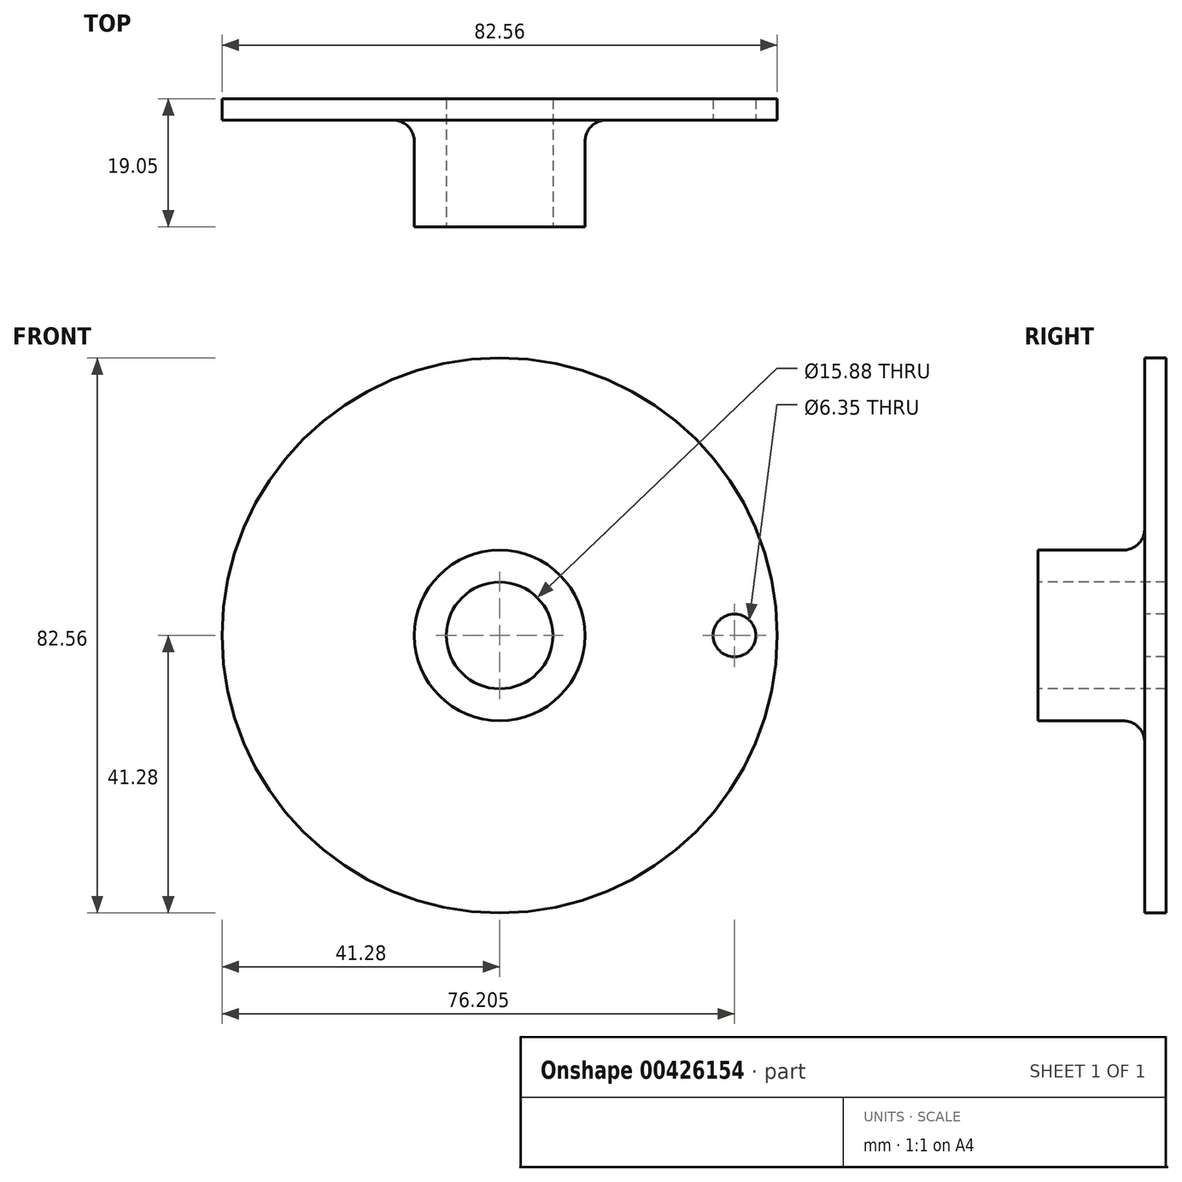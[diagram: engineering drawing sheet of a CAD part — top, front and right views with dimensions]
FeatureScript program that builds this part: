
annotation { "Feature Type Name" : "Feature", "Feature Type Description" : "" }
export const myFeature = defineFeature(function(context is Context, id is Id, definition is map)
    precondition{}
    {
        {
            var Q0;
            Q0=qCreatedBy(makeId("Right.planeOp"),FACE);
            var sketch = newSketch(context, id + "F0", { "sketchPlane" : qUnion([Q0])});
            skLineSegment(sketch, "E0.top", {"start": v(0, 41.28) * mm, "end": v(-3.18, 41.28) * mm});
            skLineSegment(sketch, "E0.left", {"start": v(0, 0) * mm, "end": v(0, 41.27) * mm});
            skLineSegment(sketch, "E0.right", {"start": v(-3.18, 12.7) * mm, "end": v(-3.18, 41.28) * mm});
            skLineSegment(sketch, "E1.bottom", {"start": v(0, 0) * mm, "end": v(-19.05, 0) * mm});
            skLineSegment(sketch, "E1.top", {"start": v(-3.18, 12.7) * mm, "end": v(-19.05, 12.7) * mm});
            skLineSegment(sketch, "E1.right", {"start": v(-19.05, 0) * mm, "end": v(-19.05, 12.7) * mm});
            skSolve(sketch);
        }
        {
            var Q0;
            Q0 = qSketchRegion(id + "F0", true);
            var Q1;
            Q1=sQuery(id+"F0.wireOp",EDGE,"E1.bottom");
            revolve(context, id + "F1", {"entities" : qUnion([Q0]), "axis" : qUnion([Q1]), "revolveType" : RevolveType.FULL});
        }
        {
            var Q0;
            Q0=makeQuery(id+"F1.opRevolve","SWEPT_FACE",FACE,{"disambiguationData":[OSD([sQuery(id+"F0.wireOp",EDGE,"E1.right")])]});
            var sketch = newSketch(context, id + "F2", { "sketchPlane" : qUnion([Q0])});
            skCircle(sketch, "E2", {"center": v(0, 0) * mm, "radius": 7.94 * mm});
            skSolve(sketch);
        }
        {
            var Q0;
            Q0 = qSketchRegion(id + "F2", true);
            extrude(context, id + "F3", {"entities" : qUnion([Q0]), "operationType" : NewBodyOperationType.REMOVE, "endBound" : BoundingType.UP_TO_NEXT, "oppositeDirection" : true, "depth" : 25.4 * mm});
        }
        {
            var Q0;
            Q0=makeQuery(id+"F1.opRevolve","SWEPT_FACE",FACE,{"disambiguationData":[OSD([sQuery(id+"F0.wireOp",EDGE,"E0.right")])]});
            var sketch = newSketch(context, id + "F4", { "sketchPlane" : qUnion([Q0])});
            skCircle(sketch, "E3", {"center": v(34.93, 0) * mm, "radius": 3.18 * mm});
            skSolve(sketch);
        }
        {
            var Q0;
            Q0 = qSketchRegion(id + "F4", true);
            extrude(context, id + "F5", {"entities" : qUnion([Q0]), "operationType" : NewBodyOperationType.REMOVE, "endBound" : BoundingType.UP_TO_NEXT, "oppositeDirection" : true, "depth" : 25.4 * mm});
        }
        {
            var Q0;
            Q0=makeQuery(id+"F1.opRevolve","SWEPT_EDGE",EDGE,{"disambiguationData":[OSD([sQuery(id+"F0.wireOp",EDGE,"E0.right"),sQuery(id+"F0.wireOp",EDGE,"E1.top")])]});
            fillet(context, id + "F6", {"entities" : qUnion([Q0]), "radius" : 3.17 * mm, "tangentPropagation" : true, "allowEdgeOverflow" : false});
        }
    });
